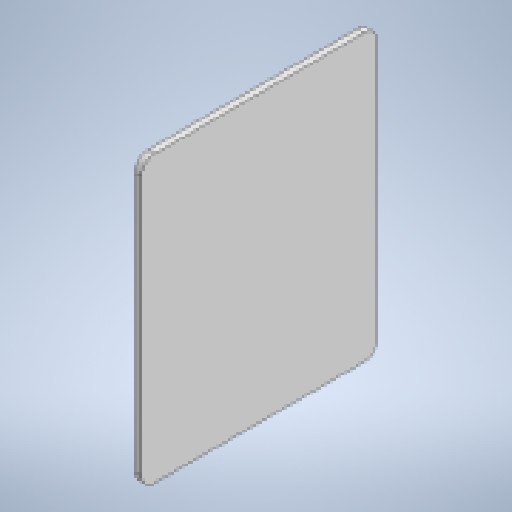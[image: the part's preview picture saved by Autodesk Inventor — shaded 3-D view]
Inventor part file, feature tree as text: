
AUTODESK INVENTOR PART (.ipt)
format: ipt  version: 2025 (Build 290162010, 162A)  size: 155,648 bytes
history: native  units: mm
features: sheet_metal_op x1, chamfer x1, sketch x1, other x1
ambient origin geometry x8: Origin, YZ Plane, XZ Plane, XY Plane, X Axis, Y Axis, Z Axis, Center Point
bodies: Solid1 (feature_tree)
feature tree (4):
  sheet_metal_op  "Face1"
  chamfer  "Corner Round1"
  sketch  "Sketch1"  dims[d0=130.0mm d1=107.582mm d2=3.048mm d3=6.0mm]
  other  "Plate1"
